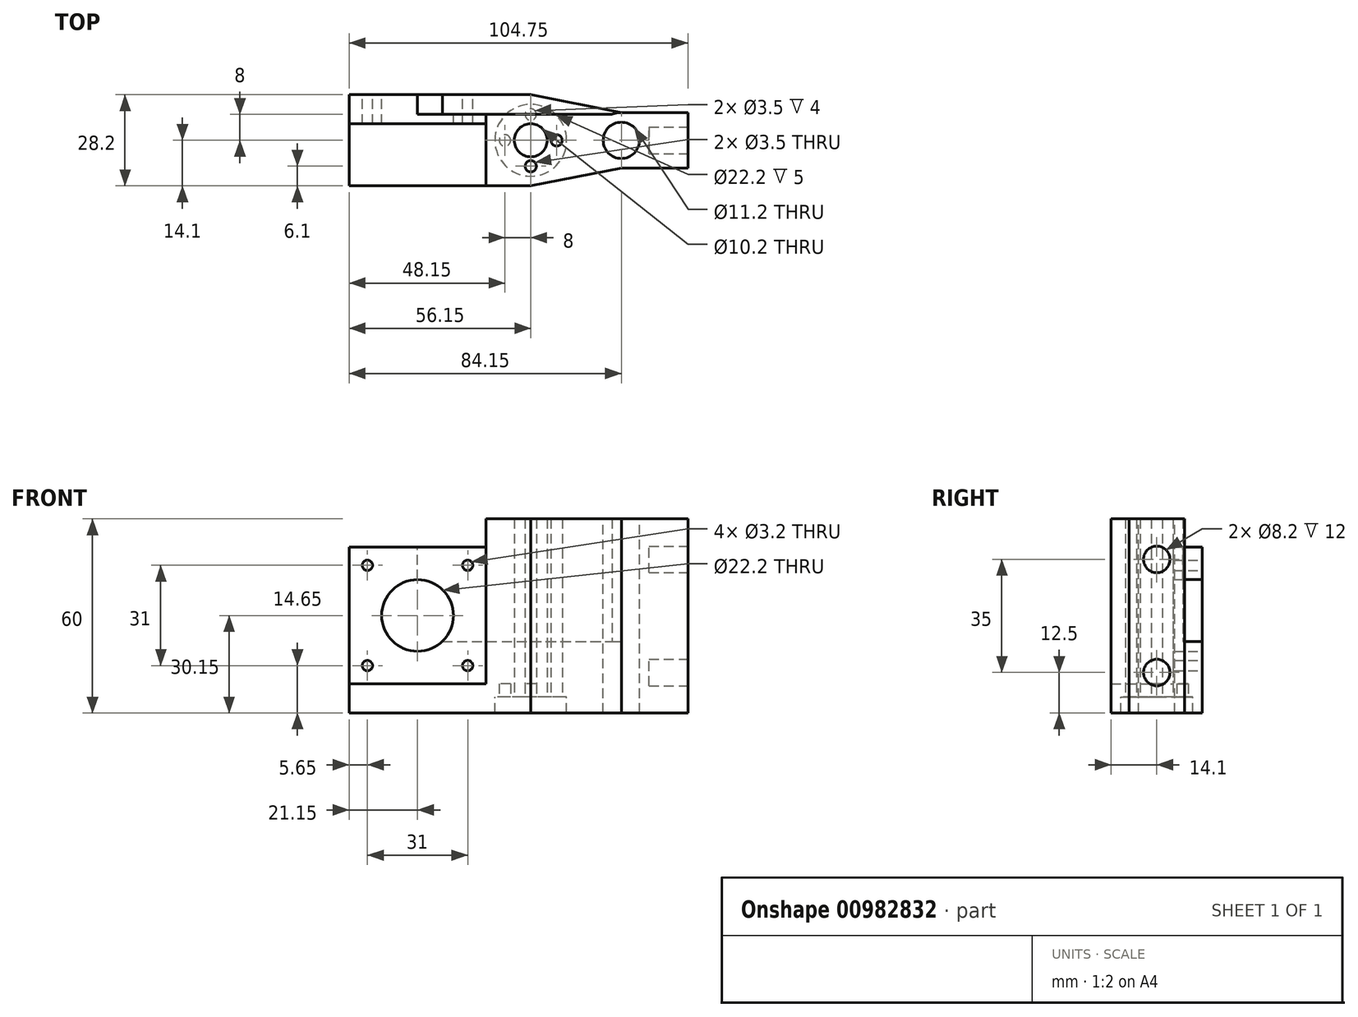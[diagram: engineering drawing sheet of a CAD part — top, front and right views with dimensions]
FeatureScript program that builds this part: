
annotation { "Feature Type Name" : "Feature", "Feature Type Description" : "" }
export const myFeature = defineFeature(function(context is Context, id is Id, definition is map)
    precondition{}
    {
        {
            var Q0;
            Q0=qCreatedBy(makeId("Top.planeOp"),FACE);
            var sketch = newSketch(context, id + "F0", { "sketchPlane" : qUnion([Q0])});
            skCircle(sketch, "E0", {"center": v(0, 0) * mm, "radius": 11.1 * mm});
            skCircle(sketch, "E1", {"center": v(28, 0) * mm, "radius": 5.6 * mm});
            skCircle(sketch, "E2", {"center": v(-8, 0) * mm, "radius": 1.75 * mm});
            skCircle(sketch, "E3", {"center": v(0, 8) * mm, "radius": 1.75 * mm});
            skCircle(sketch, "E4.MirrorC", {"center": v(0, -8) * mm, "radius": 1.75 * mm});
            skCircle(sketch, "E5.MirrorC", {"center": v(8, 0) * mm, "radius": 1.75 * mm});
            skLineSegment(sketch, "E6.bottom", {"start": v(-56.15, 5.1) * mm, "end": v(-13.85, 5.1) * mm, "construction": true});
            skLineSegment(sketch, "E6.top", {"start": v(-56.15, -29.9) * mm, "end": v(-13.85, -29.9) * mm, "construction": true});
            skLineSegment(sketch, "E6.left", {"start": v(-56.15, 5.1) * mm, "end": v(-56.15, -29.9) * mm, "construction": true});
            skLineSegment(sketch, "E6.right", {"start": v(-13.85, 5.1) * mm, "end": v(-13.85, -29.9) * mm, "construction": true});
            skLineSegment(sketch, "E7", {"start": v(-35, 5.1) * mm, "end": v(-35, 27.1) * mm, "construction": true});
            skPoint(sketch, "E8", {"position": v(-35, 11.6) * mm});
            skLineSegment(sketch, "E9", {"start": v(28, 8.6) * mm, "end": v(48.6, 8.6) * mm});
            skLineSegment(sketch, "E10", {"start": v(48.6, 8.6) * mm, "end": v(48.6, 0) * mm});
            skLineSegment(sketch, "E11", {"start": v(28, 8.6) * mm, "end": v(0, 14.1) * mm});
            skLineSegment(sketch, "E12", {"start": v(0, 14.1) * mm, "end": v(-56.15, 14.1) * mm});
            skLineSegment(sketch, "E13", {"start": v(-56.15, 14.1) * mm, "end": v(-56.15, 0) * mm});
            skLineSegment(sketch, "E14.MirrorCS", {"start": v(48.6, -8.6) * mm, "end": v(48.6, 0) * mm});
            skLineSegment(sketch, "E15.MirrorCS", {"start": v(28, -8.6) * mm, "end": v(48.6, -8.6) * mm});
            skLineSegment(sketch, "E16.MirrorCS", {"start": v(28, -8.6) * mm, "end": v(0, -14.1) * mm});
            skLineSegment(sketch, "E17.MirrorCS", {"start": v(0, -14.1) * mm, "end": v(-56.15, -14.1) * mm});
            skLineSegment(sketch, "E18.MirrorCS", {"start": v(-56.15, -14.1) * mm, "end": v(-56.15, 0) * mm});
            skCircle(sketch, "E19", {"center": v(0, 0) * mm, "radius": 5.1 * mm});
            skSolve(sketch);
        }
        {
            var Q0;
            Q0=makeQuery(id+"F0.imprint","IMPRINT",FACE,{"disambiguationData":[TD([[makeQuery(id+"F0.imprint","IMPRINT",EDGE,{"derivedFrom":sQuery(id+"F0.wireOp",EDGE,"E0")}),-1.0]])]});
            extrude(context, id + "F1", {"entities" : qUnion([Q0]), "oppositeDirection" : true, "depth" : 5 * mm, "offsetDistance" : 25 * mm});
        }
        {
            var Q0;
            Q0=makeQuery(id+"F0.imprint","IMPRINT",FACE,{"disambiguationData":[TD([[makeQuery(id+"F0.imprint","IMPRINT",EDGE,{"derivedFrom":sQuery(id+"F0.wireOp",EDGE,"E0")}),-1.0]])]});
            var Q1;
            Q1=makeQuery(id+"F0.imprint","IMPRINT",FACE,{"disambiguationData":[TD([[makeQuery(id+"F0.imprint","IMPRINT",EDGE,{"derivedFrom":sQuery(id+"F0.wireOp",EDGE,"E0")}),1.0]])]});
            extrude(context, id + "F2", {"entities" : qUnion([Q0, Q1]), "operationType" : NewBodyOperationType.ADD, "depth" : 4 * mm, "offsetDistance" : 25 * mm});
        }
        {
            var Q0;
            Q0=makeQuery(id+"F2.opExtrude","CAP_FACE",FACE,{"disambiguationData":[OSD([sQuery(id+"F0.wireOp",EDGE,"E0"),sQuery(id+"F0.wireOp",EDGE,"E1"),sQuery(id+"F0.wireOp",EDGE,"E9"),sQuery(id+"F0.wireOp",EDGE,"E10"),sQuery(id+"F0.wireOp",EDGE,"E11"),sQuery(id+"F0.wireOp",EDGE,"E12"),sQuery(id+"F0.wireOp",EDGE,"E13"),sQuery(id+"F0.wireOp",EDGE,"E14.MirrorCS"),sQuery(id+"F0.wireOp",EDGE,"E15.MirrorCS"),sQuery(id+"F0.wireOp",EDGE,"E16.MirrorCS"),sQuery(id+"F0.wireOp",EDGE,"E17.MirrorCS"),sQuery(id+"F0.wireOp",EDGE,"E18.MirrorCS")])],"isStart":false});
            var sketch = newSketch(context, id + "F3", { "sketchPlane" : qUnion([Q0])});
            skLineSegment(sketch, "E20.0", {"start": v(-56.15, 5.1) * mm, "end": v(-13.85, 5.1) * mm});
            skLineSegment(sketch, "E21.top", {"start": v(-56.15, 8.1) * mm, "end": v(-13.85, 8.1) * mm});
            skLineSegment(sketch, "E21.left", {"start": v(-56.15, 5.1) * mm, "end": v(-56.15, 8.1) * mm});
            skLineSegment(sketch, "E21.right", {"start": v(-13.85, 5.1) * mm, "end": v(-13.85, 8.1) * mm});
            skPoint(sketch, "E22.0", {"position": v(28, 0) * mm});
            skArc(sketch, "E23", {"start": v(28, 8.6) * mm, "mid": v(19.4, 0) * mm, "end": v(28, -8.6) * mm});
            skLineSegment(sketch, "E24.0", {"start": v(28, -8.6) * mm, "end": v(48.6, -8.6) * mm});
            skLineSegment(sketch, "E25.0", {"start": v(48.6, 8.6) * mm, "end": v(48.6, 0) * mm});
            skLineSegment(sketch, "E26.0", {"start": v(28, 8.6) * mm, "end": v(48.6, 8.6) * mm});
            skLineSegment(sketch, "E27.0", {"start": v(48.6, -8.6) * mm, "end": v(48.6, 0) * mm});
            skLineSegment(sketch, "E28", {"start": v(-13.85, 5.1) * mm, "end": v(21.08, 5.1) * mm});
            skLineSegment(sketch, "E29", {"start": v(-13.85, 8.1) * mm, "end": v(25.11, 8.1) * mm});
            skLineSegment(sketch, "E30", {"start": v(-13.85, 8.1) * mm, "end": v(-13.85, 14.1) * mm});
            skLineSegment(sketch, "E31", {"start": v(-13.85, 5.1) * mm, "end": v(-13.85, -14.1) * mm});
            skLineSegment(sketch, "E32", {"start": v(-13.85, -14.1) * mm, "end": v(0, -14.1) * mm});
            skLineSegment(sketch, "E33", {"start": v(0, -14.1) * mm, "end": v(28, -8.6) * mm});
            skSolve(sketch);
        }
        {
            var Q0;
            Q0=makeQuery(id+"F3.imprint","IMPRINT",FACE,{"disambiguationData":[TD([[makeQuery(id+"F3.imprint","IMPRINT",EDGE,{"derivedFrom":sQuery(id+"F3.wireOp",EDGE,"E20.0")}),1.0]])]});
            extrude(context, id + "F4", {"entities" : qUnion([Q0]), "operationType" : NewBodyOperationType.ADD, "depth" : 42.3 * mm, "offsetDistance" : 25 * mm});
        }
        {
            var Q0;
            Q0=makeQuery(id+"F4.opExtrude","SWEPT_FACE",FACE,{"disambiguationData":[OSD([sQuery(id+"F3.wireOp",EDGE,"E21.top")])]});
            var sketch = newSketch(context, id + "F5", { "sketchPlane" : qUnion([Q0])});
            skLineSegment(sketch, "E34.0.0", {"start": v(13.85, 4) * mm, "end": v(56.15, 4) * mm});
            skLineSegment(sketch, "E34.0.1", {"start": v(56.15, 4) * mm, "end": v(56.15, 46.3) * mm});
            skLineSegment(sketch, "E34.0.2", {"start": v(56.15, 46.3) * mm, "end": v(13.85, 46.3) * mm});
            skLineSegment(sketch, "E34.0.3", {"start": v(13.85, 46.3) * mm, "end": v(13.85, 4) * mm});
            skPoint(sketch, "E35", {"position": v(35, 25.15) * mm});
            skPoint(sketch, "E35.positionSnap0", {"position": v(35, 46.3) * mm});
            skPoint(sketch, "E35.positionSnap1", {"position": v(13.85, 25.15) * mm});
            skCircle(sketch, "E36", {"center": v(35, 25.15) * mm, "radius": 11.1 * mm});
            skLineSegment(sketch, "E37.bottom", {"start": v(19.5, 40.65) * mm, "end": v(50.5, 40.65) * mm, "construction": true});
            skLineSegment(sketch, "E37.top", {"start": v(19.5, 9.65) * mm, "end": v(50.5, 9.65) * mm, "construction": true});
            skLineSegment(sketch, "E37.left", {"start": v(19.5, 40.65) * mm, "end": v(19.5, 9.65) * mm, "construction": true});
            skLineSegment(sketch, "E37.right", {"start": v(50.5, 40.65) * mm, "end": v(50.5, 9.65) * mm, "construction": true});
            skCircle(sketch, "E38", {"center": v(19.5, 40.65) * mm, "radius": 1.6 * mm});
            skCircle(sketch, "E39", {"center": v(50.5, 40.65) * mm, "radius": 1.6 * mm});
            skCircle(sketch, "E40", {"center": v(50.5, 9.65) * mm, "radius": 1.6 * mm});
            skCircle(sketch, "E41", {"center": v(19.5, 9.65) * mm, "radius": 1.6 * mm});
            skLineSegment(sketch, "E42", {"start": v(35, 36.25) * mm, "end": v(35, 46.3) * mm});
            skLineSegment(sketch, "E43", {"start": v(27.3, 17.15) * mm, "end": v(13.85, 17.15) * mm});
            skSolve(sketch);
        }
        {
            var Q0;
            {var subQ0=sQuery(id+"F5.wireOp",EDGE,"E36");var subQ1=makeQuery(id+"F5.imprint","INTERSECT",VERTEX,{"derivedFrom":[subQ0,sQuery(id+"F5.wireOp",EDGE,"E42")]});Q0=makeQuery(id+"F5.imprint","IMPRINT",FACE,{"disambiguationData":[TD([[makeQuery(id+"F5.imprint","IMPRINT",EDGE,{"disambiguationData":[TD([[subQ1,-1.0]])],"derivedFrom":subQ0}),1.0]])]});}
            var Q1;
            Q1=makeQuery(id+"F5.imprint","IMPRINT",FACE,{"disambiguationData":[TD([[makeQuery(id+"F5.imprint","IMPRINT",EDGE,{"derivedFrom":sQuery(id+"F5.wireOp",EDGE,"E38")}),1.0]])]});
            var Q2;
            Q2=makeQuery(id+"F5.imprint","IMPRINT",FACE,{"disambiguationData":[TD([[makeQuery(id+"F5.imprint","IMPRINT",EDGE,{"derivedFrom":sQuery(id+"F5.wireOp",EDGE,"E41")}),1.0]])]});
            var Q3;
            Q3=makeQuery(id+"F5.imprint","IMPRINT",FACE,{"disambiguationData":[TD([[makeQuery(id+"F5.imprint","IMPRINT",EDGE,{"derivedFrom":sQuery(id+"F5.wireOp",EDGE,"E39")}),1.0]])]});
            var Q4;
            Q4=makeQuery(id+"F5.imprint","IMPRINT",FACE,{"disambiguationData":[TD([[makeQuery(id+"F5.imprint","IMPRINT",EDGE,{"derivedFrom":sQuery(id+"F5.wireOp",EDGE,"E40")}),1.0]])]});
            extrude(context, id + "F6", {"entities" : qUnion([Q0, Q1, Q2, Q3, Q4]), "operationType" : NewBodyOperationType.REMOVE, "endBound" : BoundingType.THROUGH_ALL, "oppositeDirection" : true, "depth" : 25 * mm, "offsetDistance" : 25 * mm});
        }
        {
            var Q0;
            {var subQ5=sQuery(id+"F5.wireOp",EDGE,"E34.0.0");Q0=makeQuery(id+"F5.imprint","IMPRINT",FACE,{"disambiguationData":[TD([[makeQuery(id+"F5.imprint","IMPRINT",EDGE,{"derivedFrom":subQ5}),-1.0]])]});}
            var Q1;
            {var subQ0=sQuery(id+"F0.wireOp",EDGE,"E12");Q1=makeQuery(id+"F2.boolean.opBoolean","MERGE",FACE,{"derivedFrom":[makeQuery(id+"F1.opExtrude","SWEPT_FACE",FACE,{"disambiguationData":[OSD([subQ0])]}),makeQuery(id+"F2.opExtrude","SWEPT_FACE",FACE,{"disambiguationData":[OSD([subQ0])]})]});}
            extrude(context, id + "F7", {"entities" : qUnion([Q0]), "operationType" : NewBodyOperationType.ADD, "endBound" : BoundingType.UP_TO_SURFACE, "depth" : 25 * mm, "endBoundEntityFace" : qUnion([Q1]), "offsetDistance" : 25 * mm});
        }
        {
            var Q0;
            {var subQ0=sQuery(id+"F3.wireOp",EDGE,"E24.0");Q0=makeQuery(id+"F3.imprint","IMPRINT",FACE,{"disambiguationData":[TD([[makeQuery(id+"F3.imprint","IMPRINT",EDGE,{"derivedFrom":subQ0}),1.0]])]});}
            extrude(context, id + "F8", {"entities" : qUnion([Q0]), "operationType" : NewBodyOperationType.ADD, "depth" : 51 * mm, "offsetDistance" : 25 * mm});
        }
        {
            var Q0;
            {var subQ4=sQuery(id+"F3.wireOp",EDGE,"E21.right");Q0=makeQuery(id+"F3.imprint","IMPRINT",FACE,{"disambiguationData":[TD([[makeQuery(id+"F3.imprint","IMPRINT",EDGE,{"derivedFrom":subQ4}),-1.0]])]});}
            var Q1;
            {var subQ0=sQuery(id+"F3.wireOp",EDGE,"E29");var subQ1=makeQuery(id+"F2.opExtrude","CAP_EDGE",EDGE,{"disambiguationData":[OSD([sQuery(id+"F0.wireOp",EDGE,"E3")])],"isStart":false});var subQ2=makeQuery(id+"F3.imprint","INTERSECT",VERTEX,{"disambiguationData":[OD(0.0)],"derivedFrom":[subQ1,subQ0]});Q1=makeQuery(id+"F3.imprint","IMPRINT",FACE,{"disambiguationData":[TD([[makeQuery(id+"F3.imprint","IMPRINT",EDGE,{"disambiguationData":[TD([[subQ2,-1.0]])],"derivedFrom":subQ0}),-1.0]])]});}
            var Q2;
            Q2=makeQuery(id+"F3.imprint","IMPRINT",FACE,{"disambiguationData":[TD([[makeQuery(id+"F3.imprint","IMPRINT",EDGE,{"derivedFrom":makeQuery(id+"F2.opExtrude","CAP_EDGE",EDGE,{"disambiguationData":[OSD([sQuery(id+"F0.wireOp",EDGE,"E5.MirrorC")])],"isStart":false})}),-1.0]])]});
            var Q3;
            Q3=makeQuery(id+"F3.imprint","IMPRINT",FACE,{"disambiguationData":[TD([[makeQuery(id+"F3.imprint","IMPRINT",EDGE,{"derivedFrom":makeQuery(id+"F2.opExtrude","CAP_EDGE",EDGE,{"disambiguationData":[OSD([sQuery(id+"F0.wireOp",EDGE,"E4.MirrorC")])],"isStart":false})}),-1.0]])]});
            var Q4;
            Q4=makeQuery(id+"F3.imprint","IMPRINT",FACE,{"disambiguationData":[TD([[makeQuery(id+"F3.imprint","IMPRINT",EDGE,{"derivedFrom":makeQuery(id+"F2.opExtrude","CAP_EDGE",EDGE,{"disambiguationData":[OSD([sQuery(id+"F0.wireOp",EDGE,"E2")])],"isStart":false})}),1.0]])]});
            var Q5;
            {var subQ0=sQuery(id+"F3.wireOp",EDGE,"E31");Q5=makeQuery(id+"F3.imprint","IMPRINT",FACE,{"disambiguationData":[TD([[makeQuery(id+"F3.imprint","IMPRINT",EDGE,{"derivedFrom":subQ0}),1.0]])]});}
            var Q6;
            Q6=makeQuery(id+"F8.opExtrude","CAP_FACE",FACE,{"disambiguationData":[OSD([sQuery(id+"F0.wireOp",EDGE,"E1"),sQuery(id+"F3.wireOp",EDGE,"E23"),sQuery(id+"F3.wireOp",EDGE,"E24.0"),sQuery(id+"F3.wireOp",EDGE,"E25.0"),sQuery(id+"F3.wireOp",EDGE,"E26.0"),sQuery(id+"F3.wireOp",EDGE,"E27.0")])],"isStart":false});
            extrude(context, id + "F9", {"entities" : qUnion([Q0, Q1, Q2, Q3, Q4, Q5]), "operationType" : NewBodyOperationType.ADD, "endBound" : BoundingType.UP_TO_SURFACE, "depth" : 25 * mm, "endBoundEntityFace" : qUnion([Q6]), "offsetDistance" : 25 * mm});
        }
        {
            var Q0;
            {var subQ0=sQuery(id+"F3.wireOp",EDGE,"E29");var subQ1=makeQuery(id+"F2.opExtrude","CAP_EDGE",EDGE,{"disambiguationData":[OSD([sQuery(id+"F0.wireOp",EDGE,"E3")])],"isStart":false});var subQ2=makeQuery(id+"F3.imprint","INTERSECT",VERTEX,{"disambiguationData":[OD(0.0)],"derivedFrom":[subQ1,subQ0]});Q0=makeQuery(id+"F3.imprint","IMPRINT",FACE,{"disambiguationData":[TD([[makeQuery(id+"F3.imprint","IMPRINT",EDGE,{"disambiguationData":[TD([[subQ2,-1.0]])],"derivedFrom":subQ0}),1.0]])]});}
            var Q1;
            {var subQ0=sQuery(id+"F3.wireOp",EDGE,"E30");Q1=makeQuery(id+"F3.imprint","IMPRINT",FACE,{"disambiguationData":[TD([[makeQuery(id+"F3.imprint","IMPRINT",EDGE,{"derivedFrom":subQ0}),-1.0]])]});}
            var Q2;
            Q2=makeQuery(id+"F7.opExtrude","SWEPT_FACE",FACE,{"disambiguationData":[OSD([sQuery(id+"F5.wireOp",EDGE,"E43")])]});
            extrude(context, id + "F10", {"entities" : qUnion([Q0, Q1]), "operationType" : NewBodyOperationType.ADD, "endBound" : BoundingType.UP_TO_SURFACE, "depth" : 25 * mm, "endBoundEntityFace" : qUnion([Q2]), "offsetDistance" : 25 * mm});
        }
        {
            var Q0;
            {var subQ0=sQuery(id+"F0.wireOp",EDGE,"E14.MirrorCS");var subQ1=sQuery(id+"F0.wireOp",EDGE,"E10");Q0=makeQuery(id+"F8.boolean.opBoolean","MERGE",FACE,{"derivedFrom":[makeQuery(id+"F2.boolean.opBoolean","MERGE",FACE,{"derivedFrom":[makeQuery(id+"F1.opExtrude","SWEPT_FACE",FACE,{"disambiguationData":[OSD([subQ1,subQ0])]}),makeQuery(id+"F2.opExtrude","SWEPT_FACE",FACE,{"disambiguationData":[OSD([subQ1,subQ0])]})]}),makeQuery(id+"F8.opExtrude","SWEPT_FACE",FACE,{"disambiguationData":[OSD([sQuery(id+"F3.wireOp",EDGE,"E25.0"),sQuery(id+"F3.wireOp",EDGE,"E27.0")])]})]});}
            var sketch = newSketch(context, id + "F11", { "sketchPlane" : qUnion([Q0])});
            skLineSegment(sketch, "E44", {"start": v(-8.6, 25) * mm, "end": v(3.03, 25) * mm, "construction": true});
            skCircle(sketch, "E45", {"center": v(0, 42.5) * mm, "radius": 4.1 * mm});
            skPoint(sketch, "E45.centerSnap0", {"position": v(0, 55) * mm});
            skCircle(sketch, "E46.MirrorC", {"center": v(0, 7.5) * mm, "radius": 4.1 * mm});
            skSolve(sketch);
        }
        {
            var Q0;
            Q0 = qSketchRegion(id + "F11", true);
            extrude(context, id + "F12", {"entities" : qUnion([Q0]), "operationType" : NewBodyOperationType.REMOVE, "oppositeDirection" : true, "depth" : 12 * mm, "offsetDistance" : 25 * mm});
        }
    });
